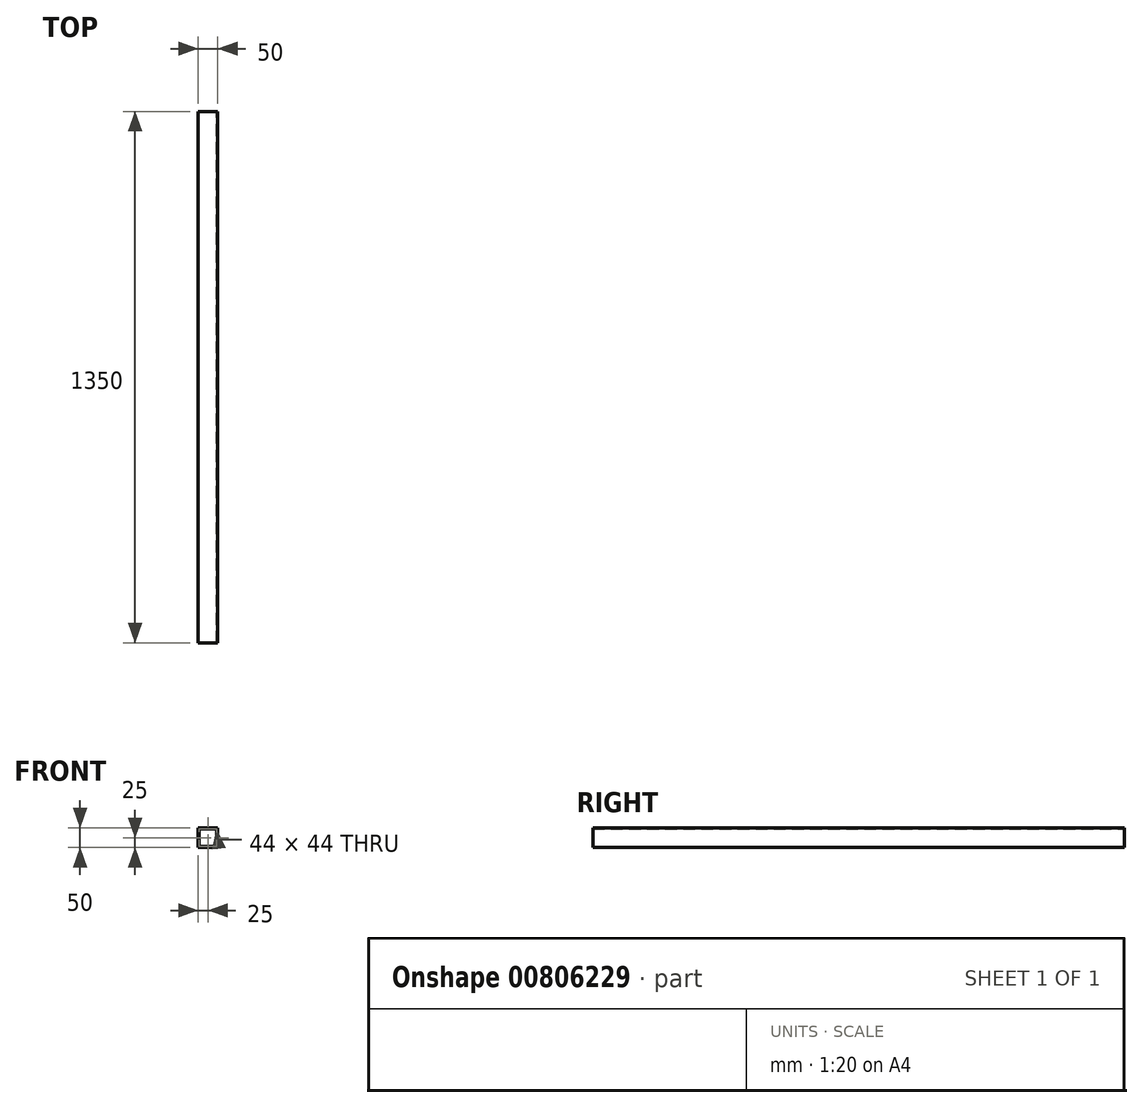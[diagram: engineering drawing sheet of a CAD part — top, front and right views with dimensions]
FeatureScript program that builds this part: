
annotation { "Feature Type Name" : "Feature", "Feature Type Description" : "" }
export const myFeature = defineFeature(function(context is Context, id is Id, definition is map)
    precondition{}
    {
        {
            var Q0;
            Q0=qCreatedBy(makeId("Front.planeOp"),FACE);
            var sketch = newSketch(context, id + "F0", { "sketchPlane" : qUnion([Q0])});
            skLineSegment(sketch, "E0.bottom", {"start": v(25, -25) * mm, "end": v(-25, -25) * mm});
            skLineSegment(sketch, "E0.top", {"start": v(25, 25) * mm, "end": v(-25, 25) * mm});
            skLineSegment(sketch, "E0.left", {"start": v(25, -25) * mm, "end": v(25, 25) * mm});
            skLineSegment(sketch, "E0.right", {"start": v(-25, -25) * mm, "end": v(-25, 25) * mm});
            skPoint(sketch, "E0.middle", {"position": v(0, 0) * mm});
            skLineSegment(sketch, "E1.0", {"start": v(22, 22) * mm, "end": v(-22, 22) * mm});
            skLineSegment(sketch, "E1.1", {"start": v(22, -22) * mm, "end": v(22, 22) * mm});
            skLineSegment(sketch, "E1.2", {"start": v(22, -22) * mm, "end": v(-22, -22) * mm});
            skLineSegment(sketch, "E1.3", {"start": v(-22, -22) * mm, "end": v(-22, 22) * mm});
            skSolve(sketch);
        }
        {
            var Q0;
            Q0=qSketchRegion(id+"F0",true);
            extrude(context, id + "F1", {"entities" : qUnion([Q0]), "depth" : 1350 * mm, "offsetDistance" : 25 * mm});
        }
    });
